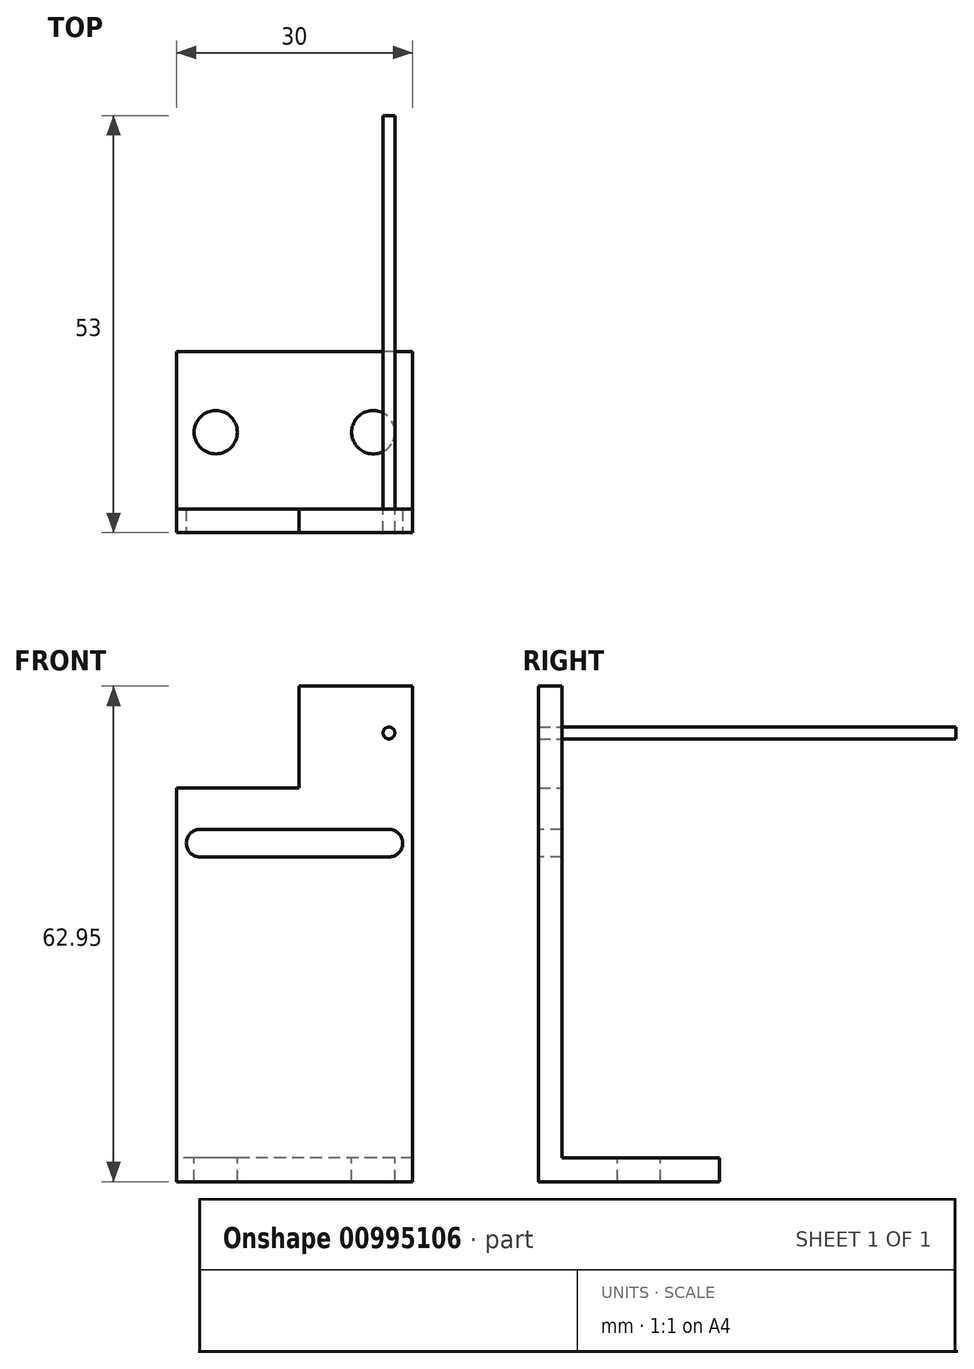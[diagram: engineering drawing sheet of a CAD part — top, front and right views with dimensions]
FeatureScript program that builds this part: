
annotation { "Feature Type Name" : "Feature", "Feature Type Description" : "" }
export const myFeature = defineFeature(function(context is Context, id is Id, definition is map)
    precondition{}
    {
        {
            var Q0;
            Q0=qCreatedBy(makeId("Front.planeOp"),FACE);
            var sketch = newSketch(context, id + "F0", { "sketchPlane" : qUnion([Q0])});
            skLineSegment(sketch, "E0.bottom", {"start": v(-12.5, 50) * mm, "end": v(17.5, 50) * mm});
            skLineSegment(sketch, "E0.top", {"start": v(-12.5, 0) * mm, "end": v(17.5, 0) * mm});
            skLineSegment(sketch, "E0.left", {"start": v(-12.5, 50) * mm, "end": v(-12.5, 0) * mm});
            skLineSegment(sketch, "E0.right", {"start": v(17.5, 50) * mm, "end": v(17.5, 0) * mm});
            skSolve(sketch);
        }
        {
            var Q0;
            Q0=qSketchRegion(id+"F0",true);
            extrude(context, id + "F1", {"entities" : qUnion([Q0]), "depth" : 3 * mm, "offsetDistance" : 25 * mm});
        }
        {
            var Q0;
            Q0=makeQuery(id+"F1.opExtrude","CAP_FACE",FACE,{"disambiguationData":[OSD([sQuery(id+"F0.wireOp",EDGE,"E0.bottom"),sQuery(id+"F0.wireOp",EDGE,"E0.top"),sQuery(id+"F0.wireOp",EDGE,"E0.left"),sQuery(id+"F0.wireOp",EDGE,"E0.right")])],"isStart":true});
            var sketch = newSketch(context, id + "F2", { "sketchPlane" : qUnion([Q0])});
            skLineSegment(sketch, "E1.bottom", {"start": v(-17.5, 0) * mm, "end": v(12.5, 0) * mm});
            skLineSegment(sketch, "E1.top", {"start": v(-17.5, 3) * mm, "end": v(12.5, 3) * mm});
            skLineSegment(sketch, "E1.left", {"start": v(-17.5, 0) * mm, "end": v(-17.5, 3) * mm});
            skLineSegment(sketch, "E1.right", {"start": v(12.5, 0) * mm, "end": v(12.5, 3) * mm});
            skSolve(sketch);
        }
        {
            var Q0;
            Q0=qSketchRegion(id+"F2",true);
            extrude(context, id + "F3", {"entities" : qUnion([Q0]), "operationType" : NewBodyOperationType.ADD, "depth" : 20 * mm, "offsetDistance" : 25 * mm});
        }
        {
            var Q0;
            Q0=makeQuery(id+"F3.opExtrude","SWEPT_FACE",FACE,{"disambiguationData":[OSD([sQuery(id+"F2.wireOp",EDGE,"E1.top")])]});
            var sketch = newSketch(context, id + "F4", { "sketchPlane" : qUnion([Q0])});
            skCircle(sketch, "E2", {"center": v(12.5, 9.76) * mm, "radius": 2.75 * mm});
            skCircle(sketch, "E3", {"center": v(-7.5, 9.76) * mm, "radius": 2.75 * mm});
            skSolve(sketch);
        }
        {
            var Q0;
            Q0=qSketchRegion(id+"F4",true);
            extrude(context, id + "F5", {"entities" : qUnion([Q0]), "operationType" : NewBodyOperationType.REMOVE, "endBound" : BoundingType.THROUGH_ALL, "oppositeDirection" : true, "depth" : 25 * mm, "offsetDistance" : 25 * mm});
        }
        {
            var Q0;
            Q0=makeQuery(id+"F1.opExtrude","CAP_FACE",FACE,{"disambiguationData":[OSD([sQuery(id+"F0.wireOp",EDGE,"E0.bottom"),sQuery(id+"F0.wireOp",EDGE,"E0.top"),sQuery(id+"F0.wireOp",EDGE,"E0.left"),sQuery(id+"F0.wireOp",EDGE,"E0.right")])],"isStart":false});
            var sketch = newSketch(context, id + "F6", { "sketchPlane" : qUnion([Q0])});
            skArc(sketch, "E4", {"start": v(-9.5, 44.75) * mm, "mid": v(-11.25, 43) * mm, "end": v(-9.5, 41.25) * mm});
            skArc(sketch, "E5", {"start": v(14.5, 41.25) * mm, "mid": v(16.25, 43) * mm, "end": v(14.5, 44.75) * mm});
            skLineSegment(sketch, "E6", {"start": v(-9.5, 44.75) * mm, "end": v(14.5, 44.75) * mm});
            skLineSegment(sketch, "E7", {"start": v(-9.5, 41.25) * mm, "end": v(14.5, 41.25) * mm});
            skSolve(sketch);
        }
        {
            var Q0;
            Q0=qSketchRegion(id+"F6",true);
            extrude(context, id + "F7", {"entities" : qUnion([Q0]), "operationType" : NewBodyOperationType.REMOVE, "endBound" : BoundingType.THROUGH_ALL, "oppositeDirection" : true, "depth" : 25 * mm, "offsetDistance" : 25 * mm});
        }
        {
            var Q0;
            Q0=makeQuery(id+"F1.opExtrude","CAP_FACE",FACE,{"disambiguationData":[OSD([sQuery(id+"F0.wireOp",EDGE,"E0.bottom"),sQuery(id+"F0.wireOp",EDGE,"E0.top"),sQuery(id+"F0.wireOp",EDGE,"E0.left"),sQuery(id+"F0.wireOp",EDGE,"E0.right")])],"isStart":true});
            var sketch = newSketch(context, id + "F8", { "sketchPlane" : qUnion([Q0])});
            skLineSegment(sketch, "E8.bottom", {"start": v(-17.5, 50) * mm, "end": v(-3.1, 50) * mm});
            skLineSegment(sketch, "E8.top", {"start": v(-17.5, 62.95) * mm, "end": v(-3.1, 62.95) * mm});
            skLineSegment(sketch, "E8.left", {"start": v(-17.5, 50) * mm, "end": v(-17.5, 62.95) * mm});
            skLineSegment(sketch, "E8.right", {"start": v(-3.1, 50) * mm, "end": v(-3.1, 62.95) * mm});
            skCircle(sketch, "E9", {"center": v(-14.5, 57) * mm, "radius": 0.75 * mm});
            skPoint(sketch, "E10", {"position": v(-14.5, 43) * mm});
            skSolve(sketch);
        }
        {
            var Q0;
            Q0=qSketchRegion(id+"F8",true);
            var Q1;
            Q1=makeQuery(id+"F1.opExtrude","CAP_FACE",FACE,{"disambiguationData":[OSD([sQuery(id+"F0.wireOp",EDGE,"E0.bottom"),sQuery(id+"F0.wireOp",EDGE,"E0.top"),sQuery(id+"F0.wireOp",EDGE,"E0.left"),sQuery(id+"F0.wireOp",EDGE,"E0.right")])],"isStart":false});
            extrude(context, id + "F9", {"entities" : qUnion([Q0]), "operationType" : NewBodyOperationType.ADD, "endBound" : BoundingType.UP_TO_SURFACE, "oppositeDirection" : true, "depth" : 25 * mm, "endBoundEntityFace" : qUnion([Q1]), "offsetDistance" : 25 * mm});
        }
        {
            var Q0;
            Q0=makeQuery(id+"F9.boolean.opBoolean","MERGE",FACE,{"derivedFrom":[makeQuery(id+"F1.opExtrude","CAP_FACE",FACE,{"disambiguationData":[OSD([sQuery(id+"F0.wireOp",EDGE,"E0.bottom"),sQuery(id+"F0.wireOp",EDGE,"E0.top"),sQuery(id+"F0.wireOp",EDGE,"E0.left"),sQuery(id+"F0.wireOp",EDGE,"E0.right")])],"isStart":true}),makeQuery(id+"F9.opExtrude","CAP_FACE",FACE,{"disambiguationData":[OSD([sQuery(id+"F8.wireOp",EDGE,"E8.bottom"),sQuery(id+"F8.wireOp",EDGE,"E8.top"),sQuery(id+"F8.wireOp",EDGE,"E8.left"),sQuery(id+"F8.wireOp",EDGE,"E8.right"),sQuery(id+"F8.wireOp",EDGE,"E9")])],"isStart":true})]});
            var sketch = newSketch(context, id + "F10", { "sketchPlane" : qUnion([Q0])});
            skCircle(sketch, "E11.0", {"center": v(-14.5, 57) * mm, "radius": 0.75 * mm});
            skSolve(sketch);
        }
        {
            var Q0;
            Q0=qSketchRegion(id+"F10",true);
            extrude(context, id + "F11", {"entities" : qUnion([Q0]), "depth" : 50 * mm, "offsetDistance" : 25 * mm});
        }
    });
